# Revit family: LENSES-EUQ0599xxWS8x0B0350
name_source: partatom
category: Leuchten
revit_build: Autodesk Revit 2017 (Build: 20160225_1515(x64)
units: mm (PartAtom-declared; Revit-internal decimal feet)

## family parameters
Basisbauteil = Fläche
Beim Laden mit Abzugskörper schneiden = Nein
Bemaßung runder Anschluss = Durchmesser verwenden
Gemeinsam genutzt = Nein
Lichtquelle = Ja
OmniClass-Nummer = 23.80.70.11
OmniClass-Titel = Luminaries for Internal Lighting
Raumberechnungspunkt = Nein
Teiletyp = Normal

## types (4) — shared parameters
Baugruppenkennzeichen = D5020200
Datei für fotometrisches Netz = LENSES-EQ0622NDWS840B0350.IES
Emissionsform beim Rendern sichtbar = Nein
Farbfilter = 16777215
Farbtemperaturverschiebung bei Dämpfen der Lampe = <Keine Auswahl>
Hersteller = RIDI Leuchten GmbH
Lampe = LED
Neigungswinkel = 90.00°
Scheinlast = 21 VA
URL = www.ridi.de
Von Breite des Rechtecks ausssenden = 516 mm  [stored 1.69291 ft]
Von Länge des Rechtecks aussenden = 470 mm  [stored 1.54199 ft]
brand = RIDI
conformity mark = CE
electrical safety class = 1
height = 60 mm  [stored 0.19685 ft]
ingress protection (IP) code = IP20
length = 599 mm  [stored 1.96522 ft]
nominal frequency = 50-60Hz
nominal voltage = 230
rated input power = 21
voltage type (AC, DC, UC) = AC
weight = 5.2kg
width = 599 mm  [stored 1.96522 ft]
zero-valued in all types: Vorgabe-Ansicht

## per-type parameters (varying)
| type | Modell | product name |
| LENSES-EUQ0599NDWS830B0350 | 0827787 | LENSES-EUQ0599NDWS830B0350 |
| LENSES-EUQ0599DAWS830B0350 | 0837787 | LENSES-EUQ0599NDWS830B0350 |
| LENSES-EUQ0599NDWS840B0350 | 0827783 | LENSES-EUQ0599NDWS840B0350 |
| LENSES-EUQ0599DAWS840B0350 | 0837783 | LENSES-EUQ0599DAWS840B0350 |

note: [stored X ft] marks values corroborated as IEEE doubles in the binary element streams (Revit-internal decimal feet)
